# Revit family: DRZ36980LAP
name_source: partatom
category: Specialty Equipment
revit_build: Autodesk Revit MEP 2014 (Build: 20130308_1515(x64)
units: mm (PartAtom-declared; Revit-internal decimal feet)

## types (1)
- DRZ36980LAP
    Annual Energy Consumption = 580 kWy/year
    Current (A) = 3
    Dedicated Evaporator & Compressor System = Yes
    Defrost Process = Frost-Free
    Depth = 25"
    Description = 36-INCH FREEZER COLUMN, LEFT-HINGE
    Door = Stainless Steel
    Door Bins = 4 ea
    Door Open Alarm = Yes
    Door Swing = Left
    ENERGY STAR® Qualified = Yes
    Freezer = 5°(-15°) to -8° (-23°)
    Freezer - Power Freeze = -8° (-23°)
    Freezer Drawer = 2 ea
    Frequency (Hz) = 60
    Full Extension Drawers at 90º Door Opening Angle = Yes
    Full Width Shelves = 3 ea
    Handle = Stainless Steel
    Height = 83 3/8"
    Hidden Compartment with Flip-up cover = 1 ea
    Ice Maker = Dual Icemaker for Standard and Cocktail Ice™
    Interior Material = SteelCool™ Stainless Steel Interior
    Lighting = 3DLighting™
    Manufacturer = Dacor
    Model = DRZ36980LAP
    Panel Ready = Yes
    Plug Type = 120 V, 3 Prong
    Power Cord Length (in.) = 78 3/4"
    Power Freeze = Yes
    Precise Cooling = Yes
    Push-To-Open™ Door Assist = Yes
    Refrigerator Gross Capacity (cu.ft.) = 21.4 cu. ft.
    Shelf Material = Tempered, Metal Trim, Spill-Proof
    Special Modes = Sabbath Mode
    Support = Plastic-Black
    Total Unit Gross Capacity (cu.ft.) - AHAM = 21.4 cu. ft.
    Unit = Stainless Steel
    Volts (V) = 115
    Width = 35 3/4"

## geometry (parser evidence)
native form markers: Sweep x1
no freeform markers — native parametric forms only
